# Revit family: monsun_r__11xtreme_ho_51fe107p480r_b295
name_source: partatom
category: Lighting Fixtures
units: mm (PartAtom-declared; Revit-internal decimal feet)

## family parameters
Cut with Voids When Loaded = No
Host = Face
Light Source = No
Part Type = Normal
Room Calculation Point = No
Round Connector Dimension = Use Diameter
Shared = No

## types (1)
- Monsun® 11Xtreme HO (1 x LED, 8000 lm, 43.2 W, 4000K)
    Apparent Load = 43 VA
    CIE Flux Codes = 47 77 93 94 100
    Color Rendering = 80
    Color Temperature = 4000K
    Default Elevation = 1800 mm
    Description = Monsun® 11Xtreme HO, damp-proof luminaire, chain hanger, primary optical cover: enclosure, of PMMA, light emission: direct distribution, primary light characteristic: symmetric, installation type: suspended mounting, surface-mounted, horizontal mounting, vertical mounting, LED, rated luminous flux: 8.000lm, luminous efficacy: 181lm/W, light colour: 840, colour temperature: 4000K, control gear: ECG, with terminal, 3-pole, max. 2.5mm², mains connection: 220..240V, AC, 50/60Hz, rated input power: 44W, luminaire housing, of glass-fibre reinforced polyester, uncoated, bright grey, length: 1.590mm, width: 90mm, height: 88mm, clip for enclosure, of stainless steel (V2A), ceiling mounting element, of stainless steel (V2A), chain hanger, of stainless steel (V2A), protection rating (complete): IP66, insulation class (complete): insulation class I (protective earthing), certification: CE, ENEC, VDE, UKCA, protection symbol: D, impact resistance: IK04, permissible operating ambient temperature: -35..+55°C, standard: EN 50419, EN 60598-2-1, corresponds to IFS (International Featured Standards) requirements for safety and quality in the food industry, for indoor or canopied outdoor use, no direct snow, no direct sun, no direct rain, packaging unit: 1 piece
    Height = 88 mm
    Lamp = 1 x LED
    Lamp Light Flux = 8000 lm
    Lamp Power = 43.2 W
    Lamp count = 1
    Length = 1590 mm
    Luminous efficacy = 185 lm/W
    Manufacturer = Siteco
    ModVariant = No
    Model = 51FE107P480R
    Mounting Place = Ceiling
    Mounting Type = Pendant
    Number of Poles = 1
    OnlyDefault = Yes
    Power Factor = 1
    Product Name = Monsun® 11Xtreme HO
    Product group = damp-proof luminaire | ceiling pendant
    ProductGroupID = 908
    Protection Class = Protection class I
    Protection Degree = IP 66
    RLX_Detail_Level = 1
    RlxData = <blob elided: 83145 chars, md5=1db9709f>
    Socket = socket
    Standby Power = 0 W
    System Light Flux = 8000 lm
    System Power = 43 W
    Type Comments = Product without accessories
    Type Image = l_1006851.jpg
    URL = http://relux.com
    VarID = ---
    Voltage = 0 V
    Weight = 0.00 kg
    Width = 90 mm

## geometry (parser evidence)
native form markers: Sweep x13
no freeform markers — native parametric forms only
